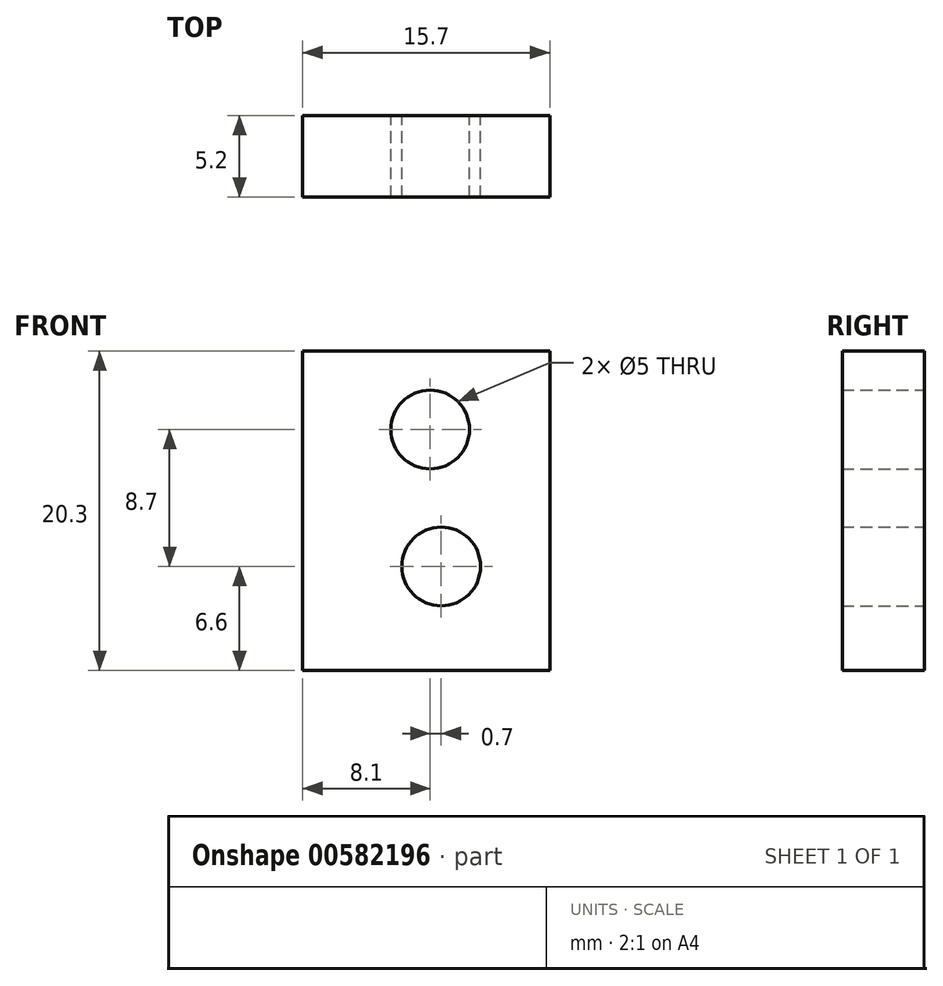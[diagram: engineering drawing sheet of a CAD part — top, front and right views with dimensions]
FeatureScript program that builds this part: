
annotation { "Feature Type Name" : "Feature", "Feature Type Description" : "" }
export const myFeature = defineFeature(function(context is Context, id is Id, definition is map)
    precondition{}
    {
        {
            var Q0;
            Q0=qCreatedBy(makeId("Front.planeOp"),FACE);
            var sketch = newSketch(context, id + "F0", { "sketchPlane" : qUnion([Q0])});
            skLineSegment(sketch, "E0.bottom", {"start": v(7.85, 10.15) * mm, "end": v(-7.85, 10.15) * mm});
            skLineSegment(sketch, "E0.top", {"start": v(7.85, -10.15) * mm, "end": v(-7.85, -10.15) * mm});
            skLineSegment(sketch, "E0.left", {"start": v(7.85, 10.15) * mm, "end": v(7.85, -10.15) * mm});
            skLineSegment(sketch, "E0.right", {"start": v(-7.85, 10.15) * mm, "end": v(-7.85, -10.15) * mm});
            skPoint(sketch, "E0.middle", {"position": v(0, 0) * mm});
            skCircle(sketch, "E1", {"center": v(0.25, 5.15) * mm, "radius": 2.5 * mm});
            skCircle(sketch, "E2", {"center": v(0.95, -3.55) * mm, "radius": 2.5 * mm});
            skSolve(sketch);
        }
        {
            var Q0;
            Q0 = qSketchRegion(id + "F0", true);
            extrude(context, id + "F1", {"entities" : qUnion([Q0]), "depth" : 5.2 * mm, "offsetDistance" : 25 * mm});
        }
    });
